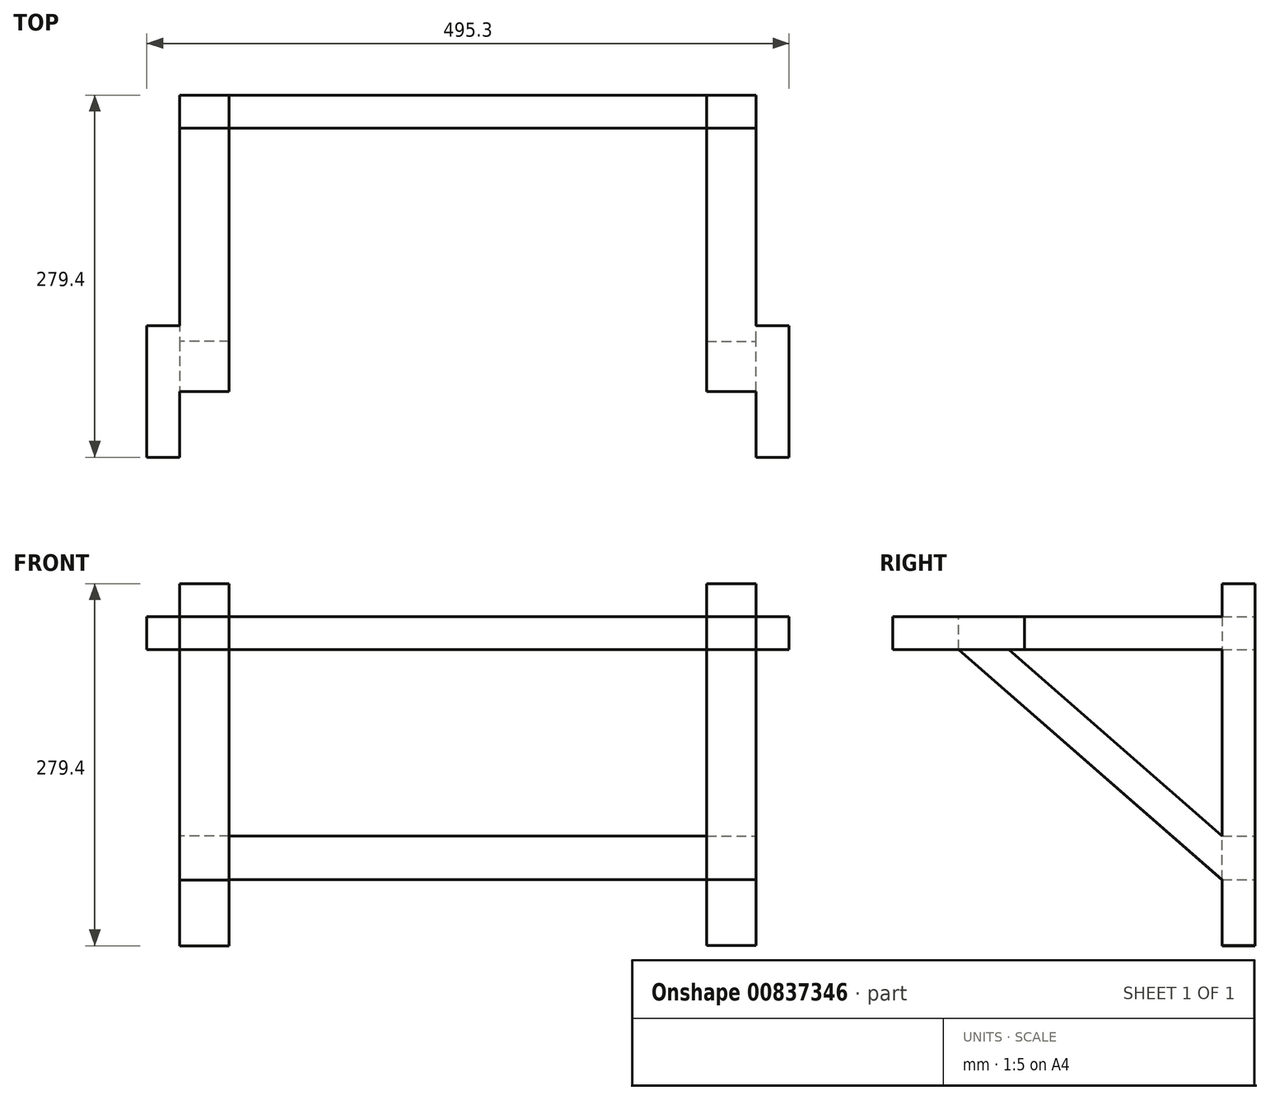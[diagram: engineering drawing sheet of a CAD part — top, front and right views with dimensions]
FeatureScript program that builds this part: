
annotation { "Feature Type Name" : "Feature", "Feature Type Description" : "" }
export const myFeature = defineFeature(function(context is Context, id is Id, definition is map)
    precondition{}
    {
        {
            var Q0;
            Q0=qCreatedBy(makeId("Front.planeOp"),FACE);
            var sketch = newSketch(context, id + "F0", { "sketchPlane" : qUnion([Q0])});
            skPoint(sketch, "E0.middle", {"position": v(0, 0) * mm});
            skLineSegment(sketch, "E1.bottom", {"start": v(-184.15, -139.7) * mm, "end": v(-222.25, -139.7) * mm});
            skLineSegment(sketch, "E1.top", {"start": v(-184.15, 139.7) * mm, "end": v(-222.25, 139.7) * mm});
            skLineSegment(sketch, "E1.left", {"start": v(-184.15, -139.7) * mm, "end": v(-184.15, 139.7) * mm});
            skLineSegment(sketch, "E1.right", {"start": v(-222.25, -139.7) * mm, "end": v(-222.25, 139.7) * mm});
            skPoint(sketch, "E1.middle", {"position": v(-203.2, 0) * mm});
            skLineSegment(sketch, "E2.bottom", {"start": v(222.25, -139.6) * mm, "end": v(184.15, -139.6) * mm});
            skLineSegment(sketch, "E2.top", {"start": v(222.25, 139.6) * mm, "end": v(184.15, 139.6) * mm});
            skLineSegment(sketch, "E2.left", {"start": v(222.25, -139.6) * mm, "end": v(222.25, 139.6) * mm});
            skLineSegment(sketch, "E2.right", {"start": v(184.15, -139.6) * mm, "end": v(184.15, 139.6) * mm});
            skPoint(sketch, "E2.middle", {"position": v(203.2, 0) * mm});
            skLineSegment(sketch, "E3.bottom", {"start": v(222.25, 88.9) * mm, "end": v(-222.25, 88.9) * mm});
            skLineSegment(sketch, "E3.top", {"start": v(222.25, 114.3) * mm, "end": v(-222.25, 114.3) * mm});
            skLineSegment(sketch, "E3.left", {"start": v(222.25, 88.9) * mm, "end": v(222.25, 114.3) * mm});
            skLineSegment(sketch, "E3.right", {"start": v(-222.25, 88.9) * mm, "end": v(-222.25, 114.3) * mm});
            skPoint(sketch, "E3.middle", {"position": v(0, 101.6) * mm});
            skLineSegment(sketch, "E4.bottom", {"start": v(-222.25, -55.04) * mm, "end": v(222.25, -55.04) * mm});
            skLineSegment(sketch, "E4.top", {"start": v(-222.25, -88.8) * mm, "end": v(222.25, -88.8) * mm});
            skLineSegment(sketch, "E4.left", {"start": v(-222.25, -55.04) * mm, "end": v(-222.25, -88.8) * mm});
            skLineSegment(sketch, "E4.right", {"start": v(222.25, -55.04) * mm, "end": v(222.25, -88.8) * mm});
            skSolve(sketch);
        }
        {
            var Q0;
            {var subQ0=sQuery(id+"F0.wireOp",EDGE,"E2.bottom");var subQ1=sQuery(id+"F0.wireOp",EDGE,"E2.left");var subQ7=sQuery(id+"F0.wireOp",EDGE,"E3.top");var subQ8=sQuery(id+"F0.wireOp",EDGE,"E1.left");var subQ9=makeQuery(id+"F0.imprint","INTERSECT",VERTEX,{"derivedFrom":[subQ8,subQ7]});var subQ10=sQuery(id+"F0.wireOp",EDGE,"E3.bottom");var subQ12=makeQuery(id+"F0.imprint","IMPRINT",EDGE,{"disambiguationData":[TD([[subQ9,1.0]])],"derivedFrom":subQ8});var subQ16=sQuery(id+"F0.wireOp",EDGE,"E4.bottom");var subQ17=makeQuery(id+"F0.imprint","INTERSECT",VERTEX,{"derivedFrom":[subQ8,subQ16]});var subQ19=makeQuery(id+"F0.imprint","IMPRINT",EDGE,{"disambiguationData":[TD([[subQ17,1.0]])],"derivedFrom":subQ8});var subQ25=sQuery(id+"F0.wireOp",EDGE,"E1.top");var subQ28=makeQuery(id+"F0.imprint","INTERSECT",VERTEX,{"derivedFrom":[subQ1,subQ10]});var subQ34=sQuery(id+"F0.wireOp",EDGE,"E1.bottom");var subQ35=makeQuery(id+"F0.imprint","INTERSECT",VERTEX,{"derivedFrom":[subQ1,subQ16]});var subQ39=sQuery(id+"F0.wireOp",EDGE,"E2.top");Q0=qUnion([makeQuery(id+"F0.imprint","IMPRINT",FACE,{"disambiguationData":[TD([[makeQuery(id+"F0.imprint","IMPRINT",EDGE,{"disambiguationData":[TD([[subQ35,-1.0]])],"derivedFrom":subQ1}),1.0]])]}),makeQuery(id+"F0.imprint","IMPRINT",FACE,{"disambiguationData":[TD([[makeQuery(id+"F0.imprint","IMPRINT",EDGE,{"derivedFrom":subQ39}),1.0]])]}),makeQuery(id+"F0.imprint","IMPRINT",FACE,{"disambiguationData":[TD([[subQ19,-1.0]])]}),makeQuery(id+"F0.imprint","IMPRINT",FACE,{"disambiguationData":[TD([[makeQuery(id+"F0.imprint","IMPRINT",EDGE,{"disambiguationData":[TD([[subQ35,1.0]])],"derivedFrom":subQ1}),1.0]])]}),makeQuery(id+"F0.imprint","IMPRINT",FACE,{"disambiguationData":[TD([[makeQuery(id+"F0.imprint","IMPRINT",EDGE,{"derivedFrom":subQ34}),-1.0]])]}),makeQuery(id+"F0.imprint","IMPRINT",FACE,{"disambiguationData":[TD([[makeQuery(id+"F0.imprint","IMPRINT",EDGE,{"disambiguationData":[TD([[subQ17,-1.0]])],"derivedFrom":subQ8}),1.0]])]}),makeQuery(id+"F0.imprint","IMPRINT",FACE,{"disambiguationData":[TD([[subQ12,1.0]])]}),makeQuery(id+"F0.imprint","IMPRINT",FACE,{"disambiguationData":[TD([[makeQuery(id+"F0.imprint","IMPRINT",EDGE,{"disambiguationData":[TD([[subQ28,-1.0]])],"derivedFrom":subQ1}),1.0]])]}),makeQuery(id+"F0.imprint","IMPRINT",FACE,{"disambiguationData":[TD([[makeQuery(id+"F0.imprint","IMPRINT",EDGE,{"derivedFrom":subQ25}),1.0]])]}),makeQuery(id+"F0.imprint","IMPRINT",FACE,{"disambiguationData":[TD([[subQ19,1.0]])]}),makeQuery(id+"F0.imprint","IMPRINT",FACE,{"disambiguationData":[TD([[subQ12,-1.0]])]}),makeQuery(id+"F0.imprint","IMPRINT",FACE,{"disambiguationData":[TD([[makeQuery(id+"F0.imprint","IMPRINT",EDGE,{"derivedFrom":subQ0}),-1.0]])]})]);}
            extrude(context, id + "F1", {"entities" : qUnion([Q0]), "depth" : 25.4 * mm, "offsetDistance" : 25.4 * mm});
        }
        {
            var Q0;
            Q0=makeQuery(id+"F1.opExtrude","CAP_FACE",FACE,{"disambiguationData":[OSD([sQuery(id+"F0.wireOp",EDGE,"E1.bottom"),sQuery(id+"F0.wireOp",EDGE,"E1.top"),sQuery(id+"F0.wireOp",EDGE,"E1.left"),sQuery(id+"F0.wireOp",EDGE,"E1.right"),sQuery(id+"F0.wireOp",EDGE,"E2.bottom"),sQuery(id+"F0.wireOp",EDGE,"E2.top"),sQuery(id+"F0.wireOp",EDGE,"E2.left"),sQuery(id+"F0.wireOp",EDGE,"E2.right"),sQuery(id+"F0.wireOp",EDGE,"E3.bottom"),sQuery(id+"F0.wireOp",EDGE,"E3.top"),sQuery(id+"F0.wireOp",EDGE,"E4.bottom"),sQuery(id+"F0.wireOp",EDGE,"E4.top")])],"isStart":false});
            var sketch = newSketch(context, id + "F2", { "sketchPlane" : qUnion([Q0])});
            skLineSegment(sketch, "E5.bottom", {"start": v(-184.15, 88.9) * mm, "end": v(-222.25, 88.9) * mm});
            skLineSegment(sketch, "E5.top", {"start": v(-184.15, 114.3) * mm, "end": v(-222.25, 114.3) * mm});
            skLineSegment(sketch, "E5.left", {"start": v(-184.15, 88.9) * mm, "end": v(-184.15, 114.3) * mm});
            skLineSegment(sketch, "E5.right", {"start": v(-222.25, 88.9) * mm, "end": v(-222.25, 114.3) * mm});
            skLineSegment(sketch, "E6.bottom", {"start": v(-184.15, 114.3) * mm, "end": v(-184.15, 114.3) * mm});
            skLineSegment(sketch, "E6.top", {"start": v(-184.15, 88.9) * mm, "end": v(-184.15, 88.9) * mm});
            skLineSegment(sketch, "E6.left", {"start": v(-184.15, 114.3) * mm, "end": v(-184.15, 88.9) * mm});
            skLineSegment(sketch, "E6.right", {"start": v(-184.15, 114.3) * mm, "end": v(-184.15, 88.9) * mm});
            skLineSegment(sketch, "E7.bottom", {"start": v(184.15, 114.3) * mm, "end": v(222.25, 114.3) * mm});
            skLineSegment(sketch, "E7.top", {"start": v(184.15, 88.9) * mm, "end": v(222.25, 88.9) * mm});
            skLineSegment(sketch, "E7.left", {"start": v(184.15, 114.3) * mm, "end": v(184.15, 88.9) * mm});
            skLineSegment(sketch, "E7.right", {"start": v(222.25, 114.3) * mm, "end": v(222.25, 88.9) * mm});
            skSolve(sketch);
        }
        {
            var Q0;
            Q0=qSketchRegion(id+"F2",true);
            extrude(context, id + "F3", {"entities" : qUnion([Q0]), "operationType" : NewBodyOperationType.ADD, "depth" : 203.2 * mm, "offsetDistance" : 25.4 * mm});
        }
        {
            var Q0;
            Q0=makeQuery(id+"F3.boolean.opBoolean","MERGE",FACE,{"derivedFrom":[makeQuery(id+"F1.opExtrude","SWEPT_FACE",FACE,{"disambiguationData":[OSD([sQuery(id+"F0.wireOp",EDGE,"E1.right")])]}),makeQuery(id+"F3.opExtrude","SWEPT_FACE",FACE,{"disambiguationData":[OSD([sQuery(id+"F2.wireOp",EDGE,"E5.right")])]})]});
            var sketch = newSketch(context, id + "F4", { "sketchPlane" : qUnion([Q0])});
            skLineSegment(sketch, "E8", {"start": v(228.6, 88.9) * mm, "end": v(25.4, -88.9) * mm});
            skLineSegment(sketch, "E9", {"start": v(25.4, -88.9) * mm, "end": v(25.4, -55.15) * mm});
            skLineSegment(sketch, "E10", {"start": v(25.4, -55.15) * mm, "end": v(190.03, 88.9) * mm});
            skLineSegment(sketch, "E11", {"start": v(190.03, 88.9) * mm, "end": v(228.6, 88.9) * mm});
            skSolve(sketch);
        }
        {
            var Q0;
            Q0=qSketchRegion(id+"F4",true);
            extrude(context, id + "F5", {"entities" : qUnion([Q0]), "operationType" : NewBodyOperationType.ADD, "oppositeDirection" : true, "depth" : 38.1 * mm, "offsetDistance" : 25.4 * mm});
        }
        {
            var Q0;
            Q0=makeQuery(id+"F3.boolean.opBoolean","MERGE",FACE,{"derivedFrom":[makeQuery(id+"F1.opExtrude","SWEPT_FACE",FACE,{"disambiguationData":[OSD([sQuery(id+"F0.wireOp",EDGE,"E2.left")])]}),makeQuery(id+"F3.opExtrude","SWEPT_FACE",FACE,{"disambiguationData":[OSD([sQuery(id+"F2.wireOp",EDGE,"E7.right")])]})]});
            var sketch = newSketch(context, id + "F6", { "sketchPlane" : qUnion([Q0])});
            skLineSegment(sketch, "E12", {"start": v(-190.02, 88.9) * mm, "end": v(-25.4, -55.05) * mm});
            skLineSegment(sketch, "E13", {"start": v(-228.6, 88.9) * mm, "end": v(-25.4, -88.8) * mm});
            skLineSegment(sketch, "E14", {"start": v(-190.02, 88.9) * mm, "end": v(-228.6, 88.9) * mm});
            skLineSegment(sketch, "E15", {"start": v(-25.4, -88.8) * mm, "end": v(-25.4, -55.05) * mm});
            skSolve(sketch);
        }
        {
            var Q0;
            Q0=qSketchRegion(id+"F6",true);
            extrude(context, id + "F7", {"entities" : qUnion([Q0]), "operationType" : NewBodyOperationType.ADD, "oppositeDirection" : true, "depth" : 38.1 * mm, "offsetDistance" : 25.4 * mm});
        }
        {
            var Q0;
            Q0=makeQuery(id+"F3.opExtrude","SWEPT_FACE",FACE,{"disambiguationData":[OSD([sQuery(id+"F2.wireOp",EDGE,"E5.top")])]});
            var sketch = newSketch(context, id + "F8", { "sketchPlane" : qUnion([Q0])});
            skLineSegment(sketch, "E16.bottom", {"start": v(-222.25, -228.6) * mm, "end": v(-247.65, -228.6) * mm});
            skLineSegment(sketch, "E16.top", {"start": v(-222.25, -177.8) * mm, "end": v(-247.65, -177.8) * mm});
            skLineSegment(sketch, "E16.left", {"start": v(-222.25, -228.6) * mm, "end": v(-222.25, -177.8) * mm});
            skLineSegment(sketch, "E16.right", {"start": v(-247.65, -228.6) * mm, "end": v(-247.65, -177.8) * mm});
            skLineSegment(sketch, "E17.MirrorCS", {"start": v(222.25, -228.6) * mm, "end": v(222.25, -177.8) * mm});
            skLineSegment(sketch, "E18.MirrorCS", {"start": v(247.65, -228.6) * mm, "end": v(247.65, -177.8) * mm});
            skLineSegment(sketch, "E19.MirrorCS", {"start": v(222.25, -177.8) * mm, "end": v(247.65, -177.8) * mm});
            skLineSegment(sketch, "E20.MirrorCS", {"start": v(222.25, -228.6) * mm, "end": v(247.65, -228.6) * mm});
            skLineSegment(sketch, "E21.bottom", {"start": v(-247.65, -228.6) * mm, "end": v(-222.25, -228.6) * mm});
            skLineSegment(sketch, "E21.top", {"start": v(-247.65, -279.4) * mm, "end": v(-222.25, -279.4) * mm});
            skLineSegment(sketch, "E21.left", {"start": v(-247.65, -228.6) * mm, "end": v(-247.65, -279.4) * mm});
            skLineSegment(sketch, "E21.right", {"start": v(-222.25, -228.6) * mm, "end": v(-222.25, -279.4) * mm});
            skLineSegment(sketch, "E22.MirrorCS", {"start": v(222.25, -228.6) * mm, "end": v(222.25, -279.4) * mm});
            skLineSegment(sketch, "E23.MirrorCS", {"start": v(247.65, -228.6) * mm, "end": v(222.25, -228.6) * mm});
            skLineSegment(sketch, "E24.MirrorCS", {"start": v(247.65, -228.6) * mm, "end": v(247.65, -279.4) * mm});
            skLineSegment(sketch, "E25.MirrorCS", {"start": v(247.65, -279.4) * mm, "end": v(222.25, -279.4) * mm});
            skSolve(sketch);
        }
        {
            var Q0;
            Q0 = qSketchRegion(id + "F8", true);
            extrude(context, id + "F9", {"entities" : qUnion([Q0]), "operationType" : NewBodyOperationType.ADD, "oppositeDirection" : true, "depth" : 25.4 * mm, "offsetDistance" : 25.4 * mm});
        }
    });
